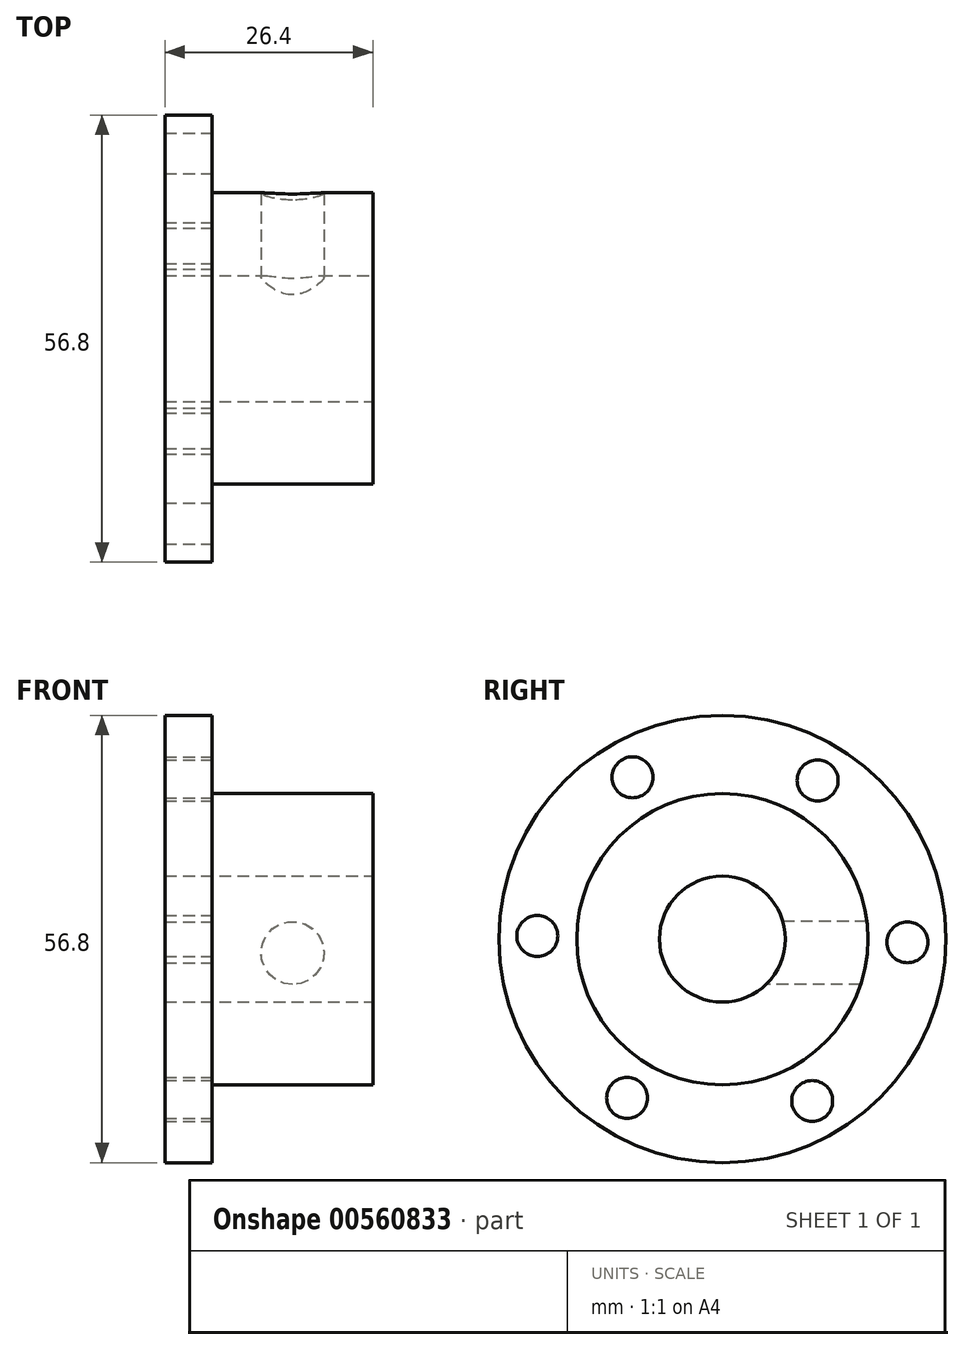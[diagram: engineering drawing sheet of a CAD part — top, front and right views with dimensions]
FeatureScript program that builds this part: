
annotation { "Feature Type Name" : "Feature", "Feature Type Description" : "" }
export const myFeature = defineFeature(function(context is Context, id is Id, definition is map)
    precondition{}
    {
        {
            var Q0;
            Q0=qCreatedBy(makeId("Front.planeOp"),FACE);
            var sketch = newSketch(context, id + "F0", { "sketchPlane" : qUnion([Q0])});
            skLineSegment(sketch, "E0", {"start": v(-32.64, -20.56) * mm, "end": v(32.64, -20.56) * mm});
            skLineSegment(sketch, "E1", {"start": v(32.64, -20.56) * mm, "end": v(-32.64, -20.56) * mm});
            skLineSegment(sketch, "E2", {"start": v(-32.64, -12.56) * mm, "end": v(-6.24, -12.56) * mm});
            skLineSegment(sketch, "E3", {"start": v(-32.64, -12.56) * mm, "end": v(-32.64, 7.84) * mm});
            skLineSegment(sketch, "E4", {"start": v(-32.64, 7.84) * mm, "end": v(-26.64, 7.84) * mm});
            skLineSegment(sketch, "E5", {"start": v(-6.24, -12.56) * mm, "end": v(-6.24, -2.06) * mm});
            skLineSegment(sketch, "E6", {"start": v(-26.64, 7.84) * mm, "end": v(-26.64, -2.06) * mm});
            skLineSegment(sketch, "E7", {"start": v(-26.64, -2.06) * mm, "end": v(-6.24, -2.06) * mm});
            skSolve(sketch);
        }
        {
            var Q0;
            Q0=qSketchRegion(id+"F0",true);
            var Q1;
            Q1=sQuery(id+"F0.wireOp",EDGE,"E1");
            revolve(context, id + "F1", {"entities" : qUnion([Q0]), "axis" : qUnion([Q1]), "revolveType" : RevolveType.FULL});
        }
        {
            var Q0;
            Q0=makeQuery(id+"F1.opRevolve","SWEPT_FACE",FACE,{"disambiguationData":[OSD([sQuery(id+"F0.wireOp",EDGE,"E6")])]});
            var sketch = newSketch(context, id + "F2", { "sketchPlane" : qUnion([Q0])});
            skCircle(sketch, "E8", {"center": v(0, -20.56) * mm, "radius": 23.52 * mm});
            skCircle(sketch, "E9", {"center": v(-11.41, 0) * mm, "radius": 2.6 * mm});
            skCircle(sketch, "E10.1.0", {"center": v(-23.52, -20.17) * mm, "radius": 2.6 * mm});
            skCircle(sketch, "E10.2.0", {"center": v(-12.1, -40.73) * mm, "radius": 2.6 * mm});
            skCircle(sketch, "E10.3.0", {"center": v(11.41, -41.13) * mm, "radius": 2.6 * mm});
            skCircle(sketch, "E10.4.0", {"center": v(23.52, -20.96) * mm, "radius": 2.6 * mm});
            skCircle(sketch, "E10.5.0", {"center": v(12.1, -0.4) * mm, "radius": 2.6 * mm});
            skSolve(sketch);
        }
        {
            var Q0;
            Q0=sQuery(id+"F2.wireOp",VERTEX,"E9.center");
            var Q1;
            Q1=sQuery(id+"F2.wireOp",VERTEX,"E10.5.0.center");
            var Q2;
            Q2=sQuery(id+"F2.wireOp",VERTEX,"E10.4.0.center");
            var Q3;
            Q3=sQuery(id+"F2.wireOp",VERTEX,"E10.3.0.center");
            var Q4;
            Q4=sQuery(id+"F2.wireOp",VERTEX,"E10.2.0.center");
            var Q5;
            Q5=sQuery(id+"F2.wireOp",VERTEX,"E10.1.0.center");
            var Q6;
            Q6=makeQuery(id+"F1.opRevolve","SWEPT_BODY",BODY,{"disambiguationData":[OSD([sQuery(id+"F0.wireOp",EDGE,"E2"),sQuery(id+"F0.wireOp",EDGE,"E3"),sQuery(id+"F0.wireOp",EDGE,"E4"),sQuery(id+"F0.wireOp",EDGE,"E5"),sQuery(id+"F0.wireOp",EDGE,"E6"),sQuery(id+"F0.wireOp",EDGE,"oNjWnfSY-uWGl-p5sd-NiaE-xDCx2udgH694")])]});
            hole(context, id + "F3", {"style" : HoleStyle.SIMPLE, "endStyle" : HoleEndStyle.THROUGH, "holeDiameter" : 5.2 * mm, "isTappedThrough" : true, "tappedDepth" : 12 * mm, "tapClearance" : 3, "locations" : qUnion([Q0, Q1, Q2, Q3, Q4, Q5]), "scope" : qUnion([Q6])});
        }
        {
            var Q0;
            Q0=qCreatedBy(makeId("Front.planeOp"),FACE);
            var sketch = newSketch(context, id + "F4", { "sketchPlane" : qUnion([Q0])});
            skCircle(sketch, "E11", {"center": v(-16.44, -22.32) * mm, "radius": 4 * mm});
            skSolve(sketch);
        }
        {
            var Q0;
            Q0=sQuery(id+"F4.wireOp",VERTEX,"E11.center");
            var Q1;
            Q1=makeQuery(id+"F1.opRevolve","SWEPT_BODY",BODY,{"disambiguationData":[OSD([sQuery(id+"F0.wireOp",EDGE,"E2"),sQuery(id+"F0.wireOp",EDGE,"E3"),sQuery(id+"F0.wireOp",EDGE,"E4"),sQuery(id+"F0.wireOp",EDGE,"E5"),sQuery(id+"F0.wireOp",EDGE,"E6"),sQuery(id+"F0.wireOp",EDGE,"E7")])]});
            hole(context, id + "F5", {"style" : HoleStyle.SIMPLE, "endStyle" : HoleEndStyle.THROUGH, "holeDiameter" : 8 * mm, "isTappedThrough" : true, "tappedDepth" : 12 * mm, "tapClearance" : 3, "locations" : qUnion([Q0]), "scope" : qUnion([Q1])});
        }
    });
